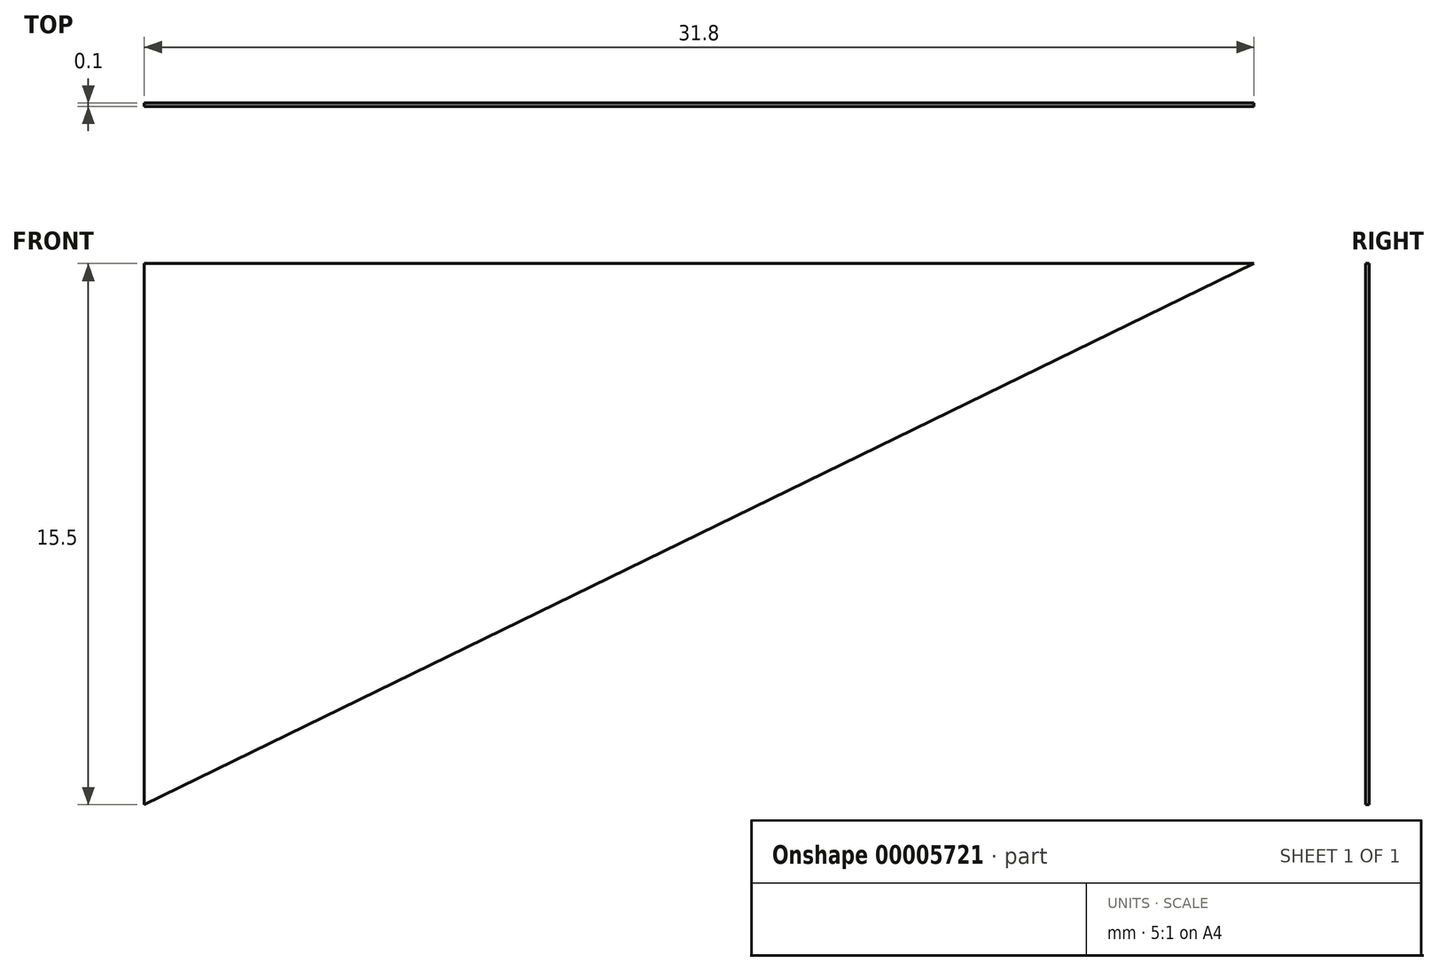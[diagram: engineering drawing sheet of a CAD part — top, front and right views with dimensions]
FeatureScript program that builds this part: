
annotation { "Feature Type Name" : "Feature", "Feature Type Description" : "" }
export const myFeature = defineFeature(function(context is Context, id is Id, definition is map)
    precondition{}
    {
        {
            var Q0;
            Q0=qCreatedBy(makeId("Front.planeOp"),FACE);
            var sketch = newSketch(context, id + "F0", { "sketchPlane" : qUnion([Q0])});
            skLineSegment(sketch, "E0.rect.bottom", {"start": v(15.9, 7.75) * mm, "end": v(-15.9, 7.75) * mm});
            skLineSegment(sketch, "E0.rect.top", {"start": v(15.9, -7.75) * mm, "end": v(-15.9, -7.75) * mm});
            skLineSegment(sketch, "E0.rect.left", {"start": v(15.9, 7.75) * mm, "end": v(15.9, -7.75) * mm});
            skLineSegment(sketch, "E0.rect.right", {"start": v(-15.9, 7.75) * mm, "end": v(-15.9, -7.75) * mm});
            skPoint(sketch, "E0.rect.middle", {"position": v(0, 0) * mm});
            skLineSegment(sketch, "E1", {"start": v(-15.9, -7.75) * mm, "end": v(15.9, 7.75) * mm});
            skSolve(sketch);
        }
        {
            var Q0;
            Q0=makeQuery(id+"F0.imprint","IMPRINT",FACE,{"disambiguationData":[TD([[makeQuery(id+"F0.imprint","IMPRINT",EDGE,{"derivedFrom":sQuery(id+"F0.wireOp",EDGE,"E0.rect.bottom")}),1.0]])]});
            extrude(context, id + "F1", {"entities" : qUnion([Q0]), "depth" : 0.1 * mm});
        }
    });
